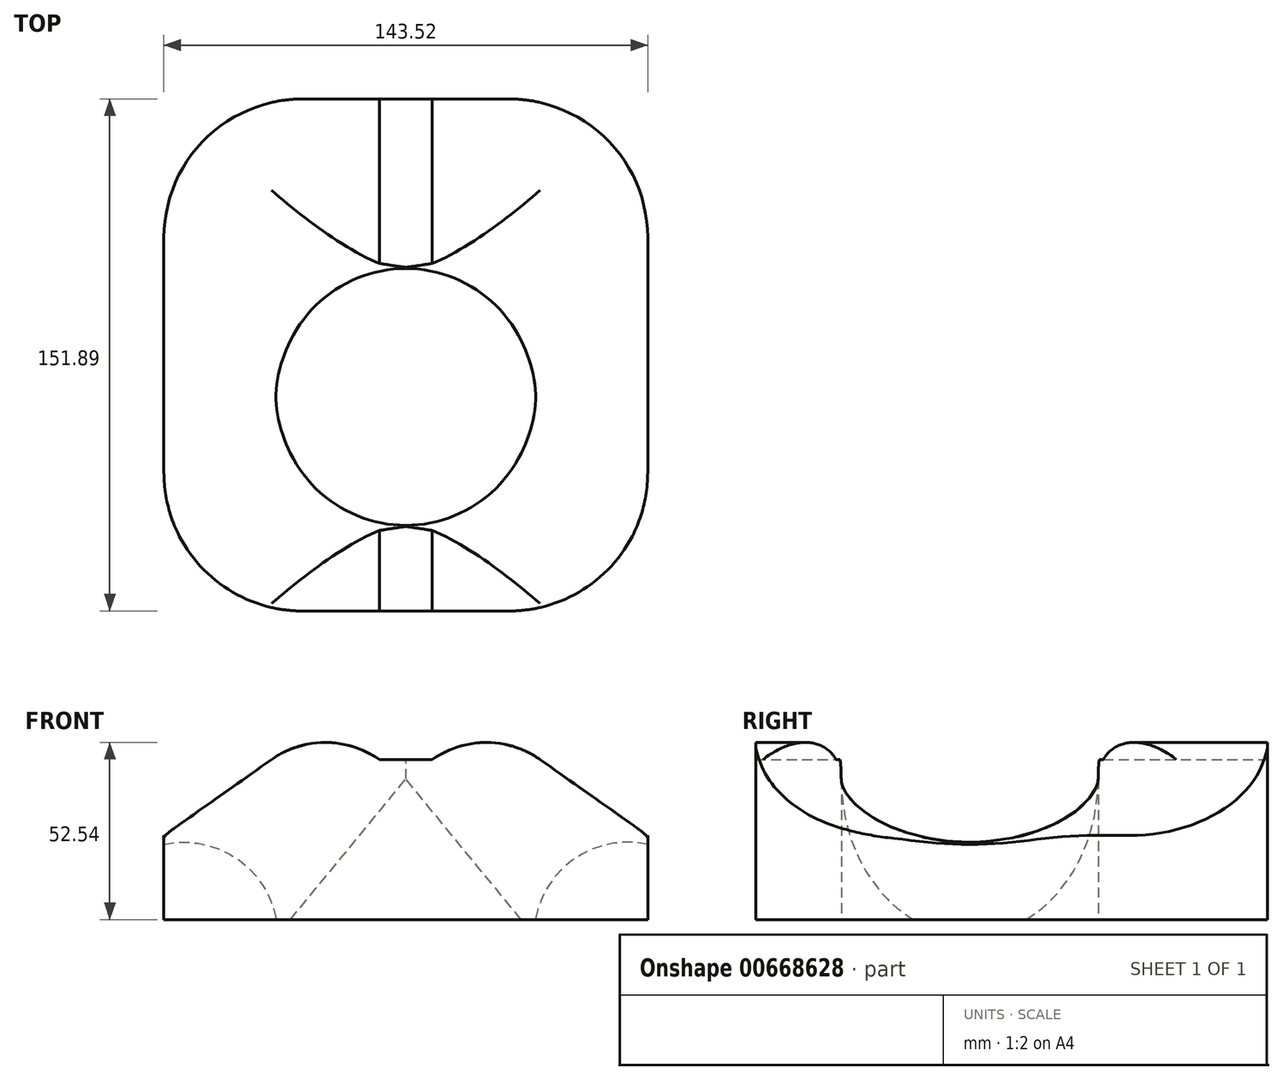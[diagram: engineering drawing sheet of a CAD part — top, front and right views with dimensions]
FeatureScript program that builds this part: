
annotation { "Feature Type Name" : "Feature", "Feature Type Description" : "" }
export const myFeature = defineFeature(function(context is Context, id is Id, definition is map)
    precondition{}
    {
        {
            var Q0;
            Q0=qCreatedBy(makeId("Front.planeOp"),FACE);
            var sketch = newSketch(context, id + "F0", { "sketchPlane" : qUnion([Q0])});
            skLineSegment(sketch, "E0", {"start": v(-71.76, 0) * mm, "end": v(-71.76, 24.93) * mm});
            skLineSegment(sketch, "E1", {"start": v(-71.76, 24.93) * mm, "end": v(-24.74, 58.11) * mm});
            skLineSegment(sketch, "E2", {"start": v(-24.74, 58.11) * mm, "end": v(-7.87, 47.5) * mm});
            skLineSegment(sketch, "E3", {"start": v(-7.87, 47.5) * mm, "end": v(0, 47.5) * mm});
            skLineSegment(sketch, "E4", {"start": v(0, 47.5) * mm, "end": v(0, 0) * mm, "construction": true});
            skLineSegment(sketch, "E5", {"start": v(-71.76, 0) * mm, "end": v(0, 0) * mm});
            skLineSegment(sketch, "E6.MirrorCS", {"start": v(7.87, 47.5) * mm, "end": v(0, 47.5) * mm});
            skLineSegment(sketch, "E7.MirrorCS", {"start": v(24.74, 58.11) * mm, "end": v(7.87, 47.5) * mm});
            skLineSegment(sketch, "E8.MirrorCS", {"start": v(71.76, 24.93) * mm, "end": v(24.74, 58.11) * mm});
            skLineSegment(sketch, "E9.MirrorCS", {"start": v(71.76, 0) * mm, "end": v(71.76, 24.93) * mm});
            skLineSegment(sketch, "E10.MirrorCS", {"start": v(71.76, 0) * mm, "end": v(0, 0) * mm});
            skSolve(sketch);
        }
        {
            var Q0;
            Q0 = qSketchRegion(id + "F0", true);
            extrude(context, id + "F1", {"entities" : qUnion([Q0]), "depth" : 151.9 * mm, "offsetDistance" : 25.4 * mm});
        }
        {
            var Q0;
            Q0=makeQuery(id+"F1.opExtrude","SWEPT_FACE",FACE,{"disambiguationData":[OSD([sQuery(id+"F0.wireOp",EDGE,"E5"),sQuery(id+"F0.wireOp",EDGE,"E10.MirrorCS")])]});
            var sketch = newSketch(context, id + "F2", { "sketchPlane" : qUnion([Q0])});
            skCircle(sketch, "E11", {"center": v(0, 88.4) * mm, "radius": 38.1 * mm});
            skSolve(sketch);
        }
        {
            var Q0;
            Q0 = qSketchRegion(id + "F2", true);
            extrude(context, id + "F3", {"entities" : qUnion([Q0]), "operationType" : NewBodyOperationType.REMOVE, "endBound" : BoundingType.THROUGH_ALL, "oppositeDirection" : true, "depth" : 25.4 * mm, "offsetDistance" : 25.4 * mm});
        }
        {
            var Q0;
            Q0=makeQuery(id+"F3.boolean.opBoolean","INTERSECT",EDGE,{"derivedFrom":[makeQuery(id+"F1.opExtrude","SWEPT_FACE",FACE,{"disambiguationData":[OSD([sQuery(id+"F0.wireOp",EDGE,"E1")])]}),makeQuery(id+"F3.opExtrude","SWEPT_FACE",FACE,{"disambiguationData":[OSD([sQuery(id+"F2.wireOp",EDGE,"E11")])]})]});
            var Q1;
            {var subQ0=sQuery(id+"F0.wireOp",EDGE,"E2");var subQ1=sQuery(id+"F0.wireOp",EDGE,"E1");Q1=makeQuery(id+"F3.boolean.opBoolean","SPLIT",EDGE,{"disambiguationData":[TD([makeQuery(id+"F1.opExtrude","CAP_FACE",FACE,{"disambiguationData":[OSD([sQuery(id+"F0.wireOp",EDGE,"E0"),subQ1,subQ0,sQuery(id+"F0.wireOp",EDGE,"E3"),sQuery(id+"F0.wireOp",EDGE,"E5"),sQuery(id+"F0.wireOp",EDGE,"E6.MirrorCS"),sQuery(id+"F0.wireOp",EDGE,"E7.MirrorCS"),sQuery(id+"F0.wireOp",EDGE,"E8.MirrorCS"),sQuery(id+"F0.wireOp",EDGE,"E9.MirrorCS"),sQuery(id+"F0.wireOp",EDGE,"E10.MirrorCS")])],"isStart":true})])],"derivedFrom":makeQuery(id+"F1.opExtrude","SWEPT_EDGE",EDGE,{"disambiguationData":[OSD([subQ1,subQ0])]})});}
            var Q2;
            {var subQ0=sQuery(id+"F0.wireOp",EDGE,"E2");var subQ1=sQuery(id+"F0.wireOp",EDGE,"E1");Q2=makeQuery(id+"F3.boolean.opBoolean","SPLIT",EDGE,{"disambiguationData":[TD([makeQuery(id+"F1.opExtrude","CAP_FACE",FACE,{"disambiguationData":[OSD([sQuery(id+"F0.wireOp",EDGE,"E0"),subQ1,subQ0,sQuery(id+"F0.wireOp",EDGE,"E3"),sQuery(id+"F0.wireOp",EDGE,"E5"),sQuery(id+"F0.wireOp",EDGE,"E6.MirrorCS"),sQuery(id+"F0.wireOp",EDGE,"E7.MirrorCS"),sQuery(id+"F0.wireOp",EDGE,"E8.MirrorCS"),sQuery(id+"F0.wireOp",EDGE,"E9.MirrorCS"),sQuery(id+"F0.wireOp",EDGE,"E10.MirrorCS")])],"isStart":false})])],"derivedFrom":makeQuery(id+"F1.opExtrude","SWEPT_EDGE",EDGE,{"disambiguationData":[OSD([subQ1,subQ0])]})});}
            var Q3;
            {var subQ0=sQuery(id+"F0.wireOp",EDGE,"E8.MirrorCS");var subQ1=sQuery(id+"F0.wireOp",EDGE,"E7.MirrorCS");Q3=makeQuery(id+"F3.boolean.opBoolean","SPLIT",EDGE,{"disambiguationData":[TD([makeQuery(id+"F1.opExtrude","CAP_FACE",FACE,{"disambiguationData":[OSD([sQuery(id+"F0.wireOp",EDGE,"E0"),sQuery(id+"F0.wireOp",EDGE,"E1"),sQuery(id+"F0.wireOp",EDGE,"E2"),sQuery(id+"F0.wireOp",EDGE,"E3"),sQuery(id+"F0.wireOp",EDGE,"E5"),sQuery(id+"F0.wireOp",EDGE,"E6.MirrorCS"),subQ1,subQ0,sQuery(id+"F0.wireOp",EDGE,"E9.MirrorCS"),sQuery(id+"F0.wireOp",EDGE,"E10.MirrorCS")])],"isStart":true})])],"derivedFrom":makeQuery(id+"F1.opExtrude","SWEPT_EDGE",EDGE,{"disambiguationData":[OSD([subQ1,subQ0])]})});}
            var Q4;
            Q4=makeQuery(id+"F3.boolean.opBoolean","INTERSECT",EDGE,{"derivedFrom":[makeQuery(id+"F1.opExtrude","SWEPT_FACE",FACE,{"disambiguationData":[OSD([sQuery(id+"F0.wireOp",EDGE,"E8.MirrorCS")])]}),makeQuery(id+"F3.opExtrude","SWEPT_FACE",FACE,{"disambiguationData":[OSD([sQuery(id+"F2.wireOp",EDGE,"E11")])]})]});
            var Q5;
            {var subQ0=sQuery(id+"F0.wireOp",EDGE,"E8.MirrorCS");var subQ1=sQuery(id+"F0.wireOp",EDGE,"E7.MirrorCS");Q5=makeQuery(id+"F3.boolean.opBoolean","SPLIT",EDGE,{"disambiguationData":[TD([makeQuery(id+"F1.opExtrude","CAP_FACE",FACE,{"disambiguationData":[OSD([sQuery(id+"F0.wireOp",EDGE,"E0"),sQuery(id+"F0.wireOp",EDGE,"E1"),sQuery(id+"F0.wireOp",EDGE,"E2"),sQuery(id+"F0.wireOp",EDGE,"E3"),sQuery(id+"F0.wireOp",EDGE,"E5"),sQuery(id+"F0.wireOp",EDGE,"E6.MirrorCS"),subQ1,subQ0,sQuery(id+"F0.wireOp",EDGE,"E9.MirrorCS"),sQuery(id+"F0.wireOp",EDGE,"E10.MirrorCS")])],"isStart":false})])],"derivedFrom":makeQuery(id+"F1.opExtrude","SWEPT_EDGE",EDGE,{"disambiguationData":[OSD([subQ1,subQ0])]})});}
            fillet(context, id + "F4", {"entities" : qUnion([Q0, Q1, Q2, Q3, Q4, Q5]), "radius" : 27.68 * mm, "tangentPropagation" : true, "allowEdgeOverflow" : false});
        }
        {
            var Q0;
            Q0=makeQuery(id+"F1.opExtrude","CAP_EDGE",EDGE,{"disambiguationData":[OSD([sQuery(id+"F0.wireOp",EDGE,"E9.MirrorCS")])],"isStart":false});
            var Q1;
            Q1=makeQuery(id+"F1.opExtrude","CAP_EDGE",EDGE,{"disambiguationData":[OSD([sQuery(id+"F0.wireOp",EDGE,"E9.MirrorCS")])],"isStart":true});
            var Q2;
            Q2=makeQuery(id+"F1.opExtrude","CAP_EDGE",EDGE,{"disambiguationData":[OSD([sQuery(id+"F0.wireOp",EDGE,"E0")])],"isStart":true});
            var Q3;
            Q3=makeQuery(id+"F1.opExtrude","CAP_EDGE",EDGE,{"disambiguationData":[OSD([sQuery(id+"F0.wireOp",EDGE,"E0")])],"isStart":false});
            fillet(context, id + "F5", {"entities" : qUnion([Q0, Q1, Q2, Q3]), "radius" : 41.1 * mm, "tangentPropagation" : true, "allowEdgeOverflow" : false});
        }
        {
            var Q0;
            Q0=qCreatedBy(makeId("Top.planeOp"),FACE);
            cPlane(context, id + "F6", {"entities" : qUnion([Q0]), "cplaneType" : CPlaneType.OFFSET, "offset" : 3.17 * mm, "oppositeDirection" : true, "width" : 152.4 * mm, "height" : 152.4 * mm});
        }
    });
